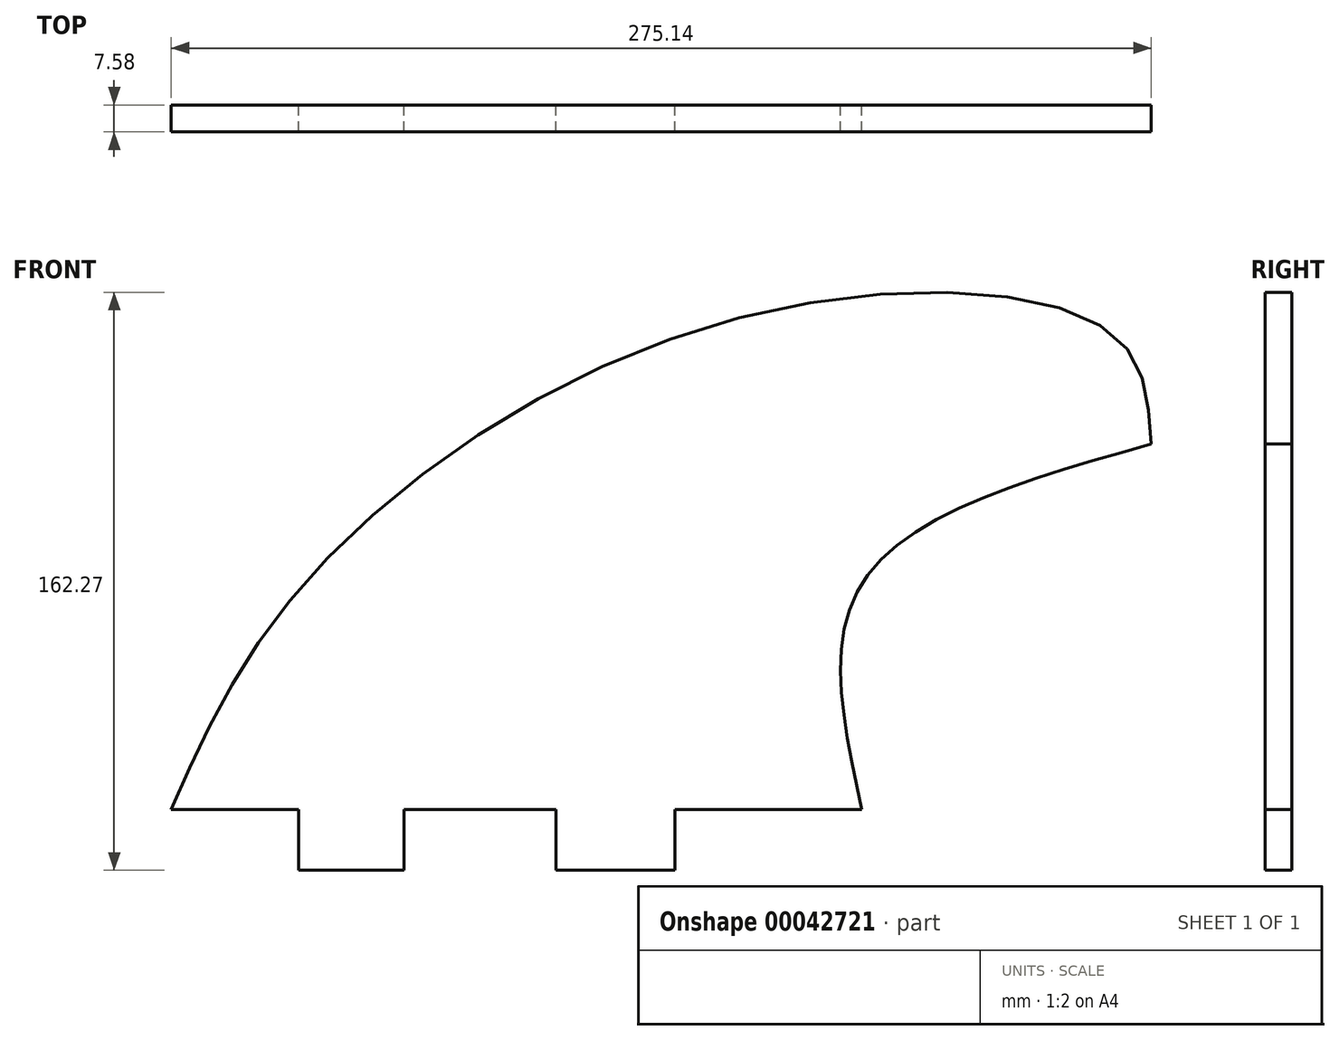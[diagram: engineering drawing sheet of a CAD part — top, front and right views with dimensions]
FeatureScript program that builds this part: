
annotation { "Feature Type Name" : "Feature", "Feature Type Description" : "" }
export const myFeature = defineFeature(function(context is Context, id is Id, definition is map)
    precondition{}
    {
        {
            var Q0;
            Q0=qCreatedBy(makeId("Front.planeOp"),FACE);
            var sketch = newSketch(context, id + "F0", { "sketchPlane" : qUnion([Q0])});
            skLineSegment(sketch, "E0", {"start": v(-75.7, -63.5) * mm, "end": v(-39.89, -63.5) * mm});
            skLineSegment(sketch, "E1", {"start": v(-39.89, -63.5) * mm, "end": v(-39.89, -80.58) * mm});
            skLineSegment(sketch, "E2", {"start": v(-39.89, -80.58) * mm, "end": v(-10.38, -80.58) * mm});
            skLineSegment(sketch, "E3", {"start": v(-10.38, -80.58) * mm, "end": v(-10.38, -63.5) * mm});
            skLineSegment(sketch, "E4", {"start": v(-10.38, -63.5) * mm, "end": v(32.36, -63.5) * mm});
            skLineSegment(sketch, "E5", {"start": v(32.36, -63.5) * mm, "end": v(32.36, -80.58) * mm});
            skLineSegment(sketch, "E6", {"start": v(32.36, -80.58) * mm, "end": v(65.73, -80.58) * mm});
            skLineSegment(sketch, "E7", {"start": v(65.73, -80.58) * mm, "end": v(65.73, -63.5) * mm});
            skLineSegment(sketch, "E8", {"start": v(65.73, -63.5) * mm, "end": v(118.23, -63.5) * mm});
            skFitSpline(sketch, "E9", {"points": [v(118.23, -63.5) * mm, v(118.23, 0) * mm, v(199.44, 39.09) * mm], "startDerivative": vector(-34.08, 154.48) * mm, "endDerivative": vector(189.97, 53.61) * mm});
            skFitSpline(sketch, "E10", {"points": [v(-75.7, -63.5) * mm, v(-38.3, 0) * mm, v(81.02, 73.82) * mm, v(188.61, 69.99) * mm, v(199.44, 39.09) * mm], "startDerivative": vector(118.55, 267.9) * mm, "endDerivative": vector(11.63, -221.62) * mm});
            skSolve(sketch);
        }
        {
            var Q0;
            Q0=makeQuery(id+"F0.imprint","IMPRINT",FACE,{"disambiguationData":[TD([[makeQuery(id+"F0.imprint","IMPRINT",EDGE,{"derivedFrom":sQuery(id+"F0.wireOp",EDGE,"E0")}),1.0]])]});
            extrude(context, id + "F1", {"entities" : qUnion([Q0]), "depth" : 7.58 * mm});
        }
    });
